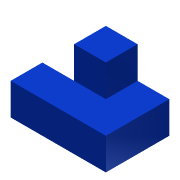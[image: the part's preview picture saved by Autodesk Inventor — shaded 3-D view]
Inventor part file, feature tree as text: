
AUTODESK INVENTOR PART (.ipt)
format: ipt  version: 2015 (Build 190159000, 159)  size: 91,648 bytes
history: native  units: in
note: dims shown in document units (in); Inventor stores cm internally (conversion verified against a paired STEP export)
features: extrude x2, sketch x2
ambient origin geometry x8: Origin, YZ Plane, XZ Plane, XY Plane, X Axis, Y Axis, Z Axis, Center Point
bodies: Solid1 (feature_tree)
feature tree (4):
  extrude  "Extrusion1"  Depth=1.0in
  extrude  "Extrusion2"  Depth=1.0in
  sketch  "Sketch1"  dims[d0=3.0in d1=1.0in]
  sketch  "Sketch2"  dims[d2=1.0in d3=1.0in d4=2.0in d5=1.0in d6=0.0in d7=1.0in d8=1.0in d9=0.0in]
